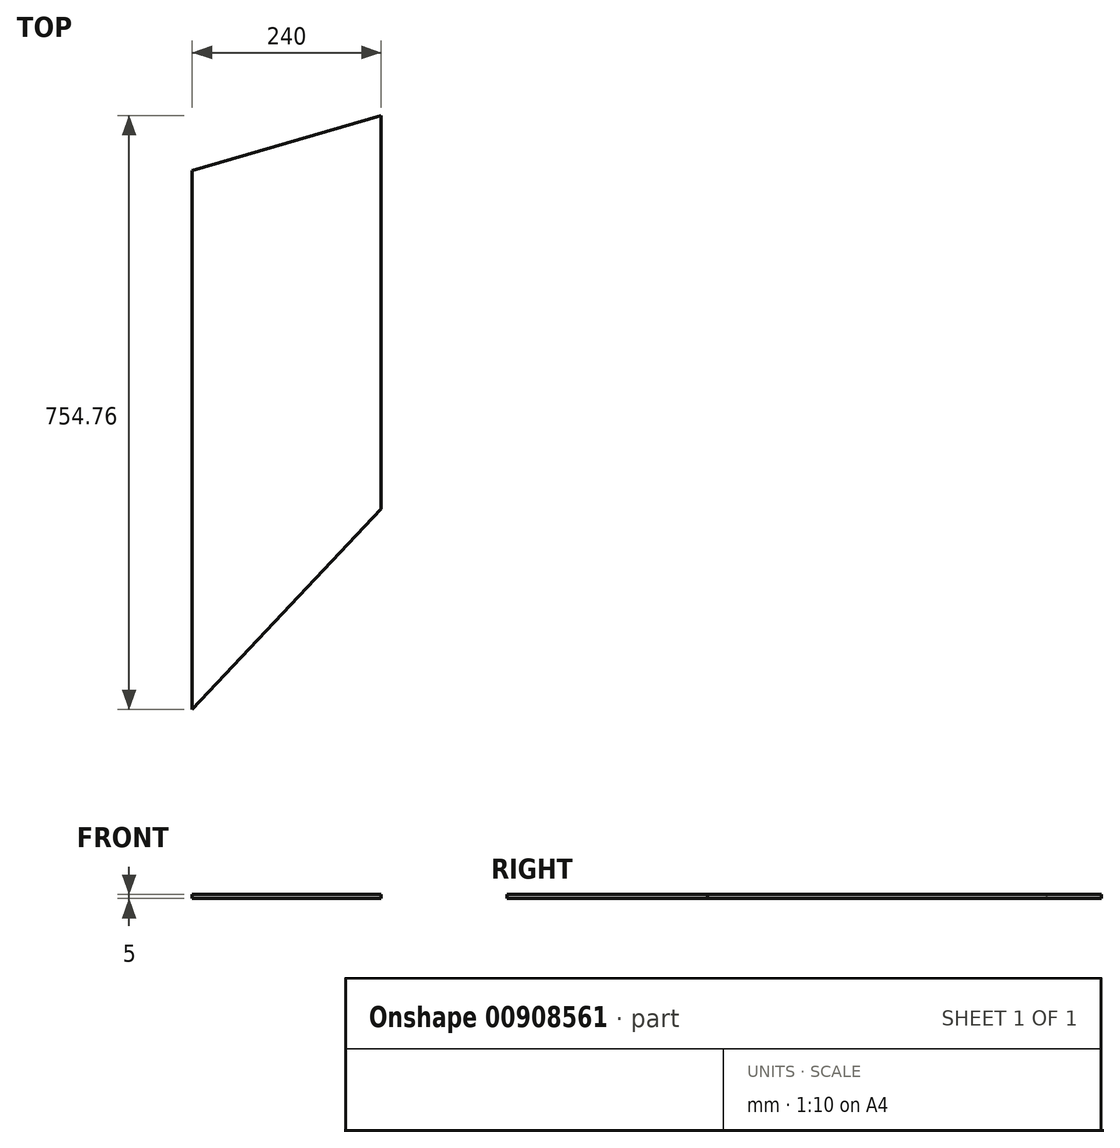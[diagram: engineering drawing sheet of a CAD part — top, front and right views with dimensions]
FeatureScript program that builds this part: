
annotation { "Feature Type Name" : "Feature", "Feature Type Description" : "" }
export const myFeature = defineFeature(function(context is Context, id is Id, definition is map)
    precondition{}
    {
        {
            var Q0;
            Q0=qCreatedBy(makeId("Top.planeOp"),FACE);
            var sketch = newSketch(context, id + "F0", { "sketchPlane" : qUnion([Q0])});
            skLineSegment(sketch, "E0.top", {"start": v(120, 377.38) * mm, "end": v(-120, 377.38) * mm, "construction": true});
            skLineSegment(sketch, "E0.left", {"start": v(120, -122.62) * mm, "end": v(120, 377.38) * mm});
            skLineSegment(sketch, "E0.right", {"start": v(-120, -377.38) * mm, "end": v(-120, 307.38) * mm});
            skPoint(sketch, "E0.middle", {"position": v(0, 0) * mm});
            skLineSegment(sketch, "E1", {"start": v(-120, -377.38) * mm, "end": v(120, -122.62) * mm});
            skPoint(sketch, "E2.orphan", {"position": v(120, -377.38) * mm});
            skLineSegment(sketch, "E3", {"start": v(120, 377.38) * mm, "end": v(-120, 307.38) * mm});
            skSolve(sketch);
        }
        {
            var Q0;
            Q0 = qSketchRegion(id + "F0", true);
            extrude(context, id + "F1", {"entities" : qUnion([Q0]), "depth" : 5 * mm, "offsetDistance" : 25 * mm});
        }
    });
